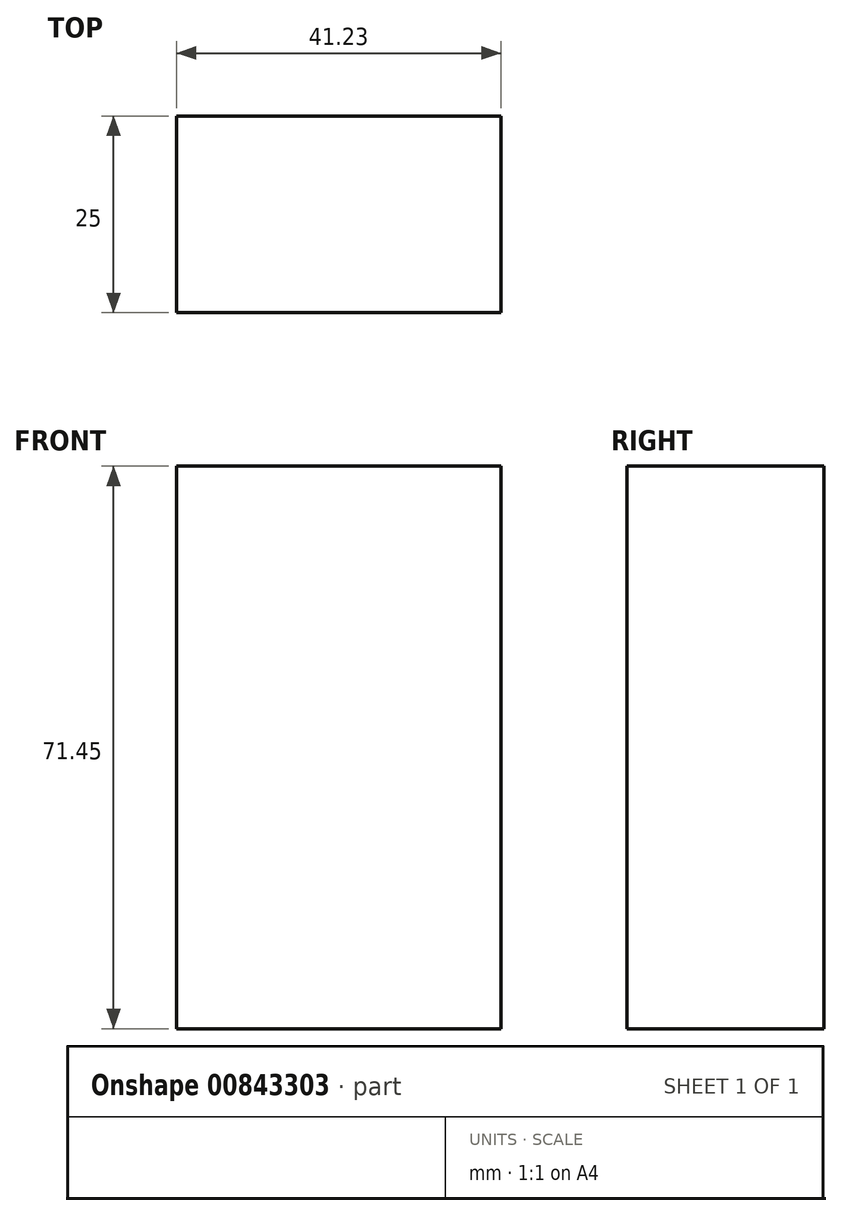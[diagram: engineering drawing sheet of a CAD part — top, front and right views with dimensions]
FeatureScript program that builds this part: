
annotation { "Feature Type Name" : "Feature", "Feature Type Description" : "" }
export const myFeature = defineFeature(function(context is Context, id is Id, definition is map)
    precondition{}
    {
        {
            var Q0;
            Q0=qCreatedBy(makeId("Front.planeOp"),FACE);
            var sketch = newSketch(context, id + "F0", { "sketchPlane" : qUnion([Q0])});
            skLineSegment(sketch, "E0.bottom", {"start": v(-109.34, 39.24) * mm, "end": v(-68.11, 39.24) * mm});
            skLineSegment(sketch, "E0.top", {"start": v(-109.34, -32.21) * mm, "end": v(-68.11, -32.21) * mm});
            skLineSegment(sketch, "E0.left", {"start": v(-109.34, 39.24) * mm, "end": v(-109.34, -32.21) * mm});
            skLineSegment(sketch, "E0.right", {"start": v(-68.11, 39.24) * mm, "end": v(-68.11, -32.21) * mm});
            skSolve(sketch);
        }
        {
            var Q0;
            Q0 = qSketchRegion(id + "F0", true);
            extrude(context, id + "F1", {"entities" : qUnion([Q0]), "depth" : 25 * mm, "offsetDistance" : 25 * mm});
        }
    });
